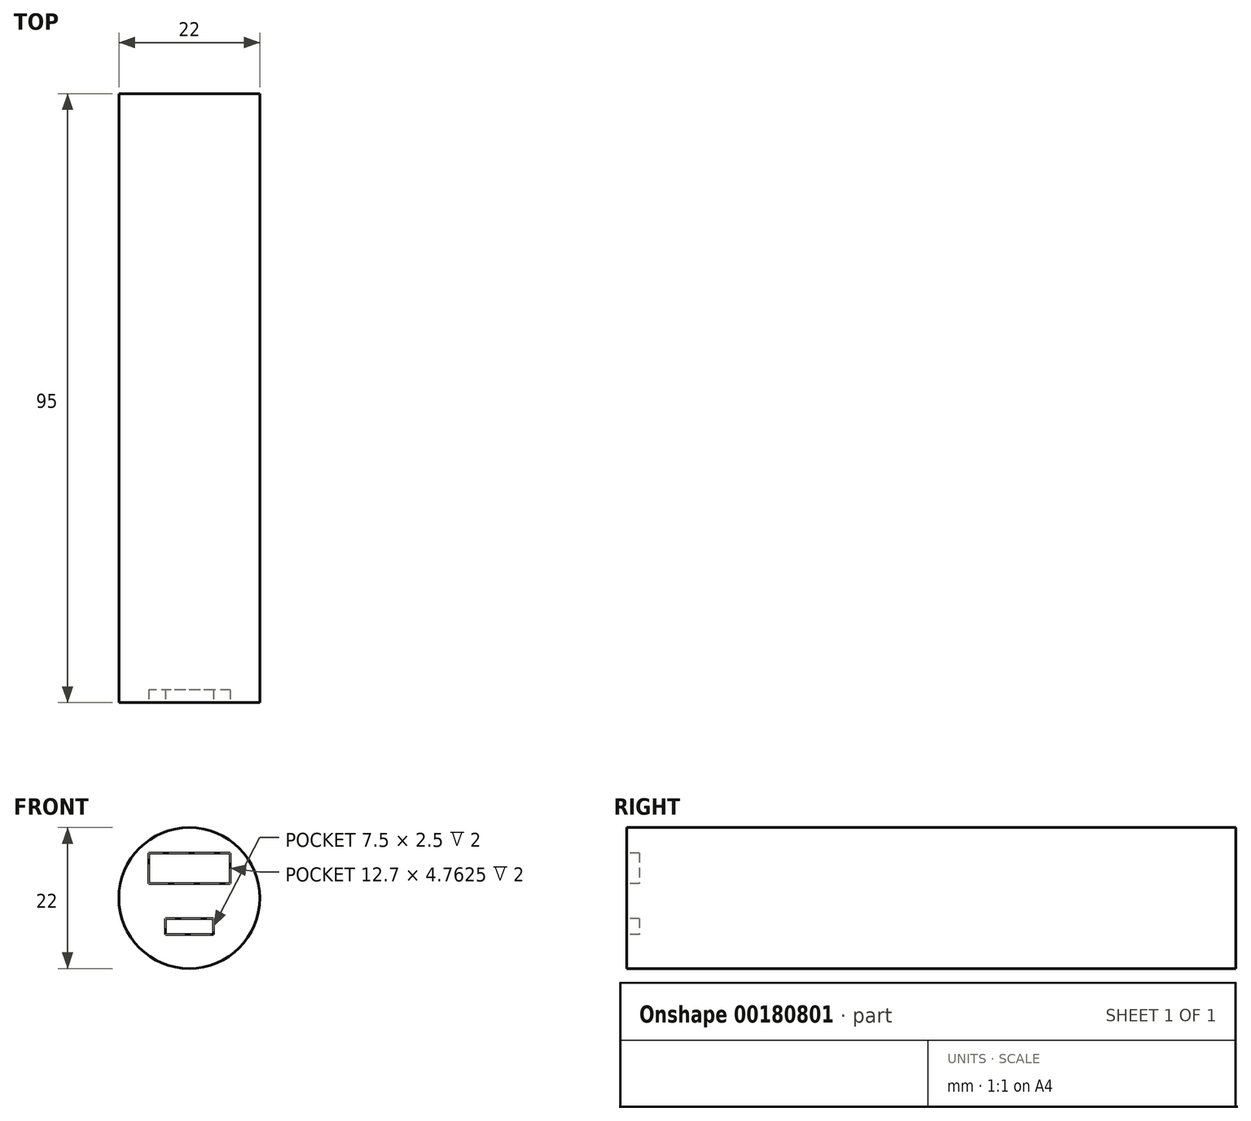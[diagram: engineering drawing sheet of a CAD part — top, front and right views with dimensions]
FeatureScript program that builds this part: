
annotation { "Feature Type Name" : "Feature", "Feature Type Description" : "" }
export const myFeature = defineFeature(function(context is Context, id is Id, definition is map)
    precondition{}
    {
        {
            var Q0;
            Q0=qCreatedBy(makeId("Front.planeOp"),FACE);
            var sketch = newSketch(context, id + "F0", { "sketchPlane" : qUnion([Q0])});
            skPoint(sketch, "E0.middle", {"position": v(0, 0) * mm});
            skCircle(sketch, "E1", {"center": v(0, 0) * mm, "radius": 11 * mm});
            skSolve(sketch);
        }
        {
            var Q0;
            Q0=makeQuery(id+"F0.imprint","IMPRINT",FACE,{"disambiguationData":[TD([[makeQuery(id+"F0.imprint","IMPRINT",EDGE,{"derivedFrom":sQuery(id+"F0.wireOp",EDGE,"E0.bottom")}),1.0]])]});
            var Q1;
            Q1=makeQuery(id+"F0.imprint","IMPRINT",FACE,{"disambiguationData":[TD([[makeQuery(id+"F0.imprint","IMPRINT",EDGE,{"derivedFrom":sQuery(id+"F0.wireOp",EDGE,"E1")}),1.0]])]});
            extrude(context, id + "F1", {"entities" : qUnion([Q0, Q1]), "depth" : 95 * mm, "offsetDistance" : 25 * mm});
        }
        {
            var Q0;
            Q0=makeQuery(id+"F1.opExtrude","CAP_FACE",FACE,{"disambiguationData":[OSD([sQuery(id+"F0.wireOp",EDGE,"E1")])],"isStart":false});
            var sketch = newSketch(context, id + "F2", { "sketchPlane" : qUnion([Q0])});
            skLineSegment(sketch, "E2.bottom", {"start": v(6.35, 7.02) * mm, "end": v(-6.35, 7.02) * mm});
            skLineSegment(sketch, "E2.top", {"start": v(6.35, 2.26) * mm, "end": v(-6.35, 2.26) * mm});
            skLineSegment(sketch, "E2.left", {"start": v(6.35, 7.02) * mm, "end": v(6.35, 2.26) * mm});
            skLineSegment(sketch, "E2.right", {"start": v(-6.35, 7.02) * mm, "end": v(-6.35, 2.26) * mm});
            skPoint(sketch, "E2.middle", {"position": v(0, 4.64) * mm});
            skLineSegment(sketch, "E3.bottom", {"start": v(3.75, -3.2) * mm, "end": v(-3.75, -3.2) * mm});
            skLineSegment(sketch, "E3.top", {"start": v(3.75, -5.7) * mm, "end": v(-3.75, -5.7) * mm});
            skLineSegment(sketch, "E3.left", {"start": v(3.75, -3.2) * mm, "end": v(3.75, -5.7) * mm});
            skLineSegment(sketch, "E3.right", {"start": v(-3.75, -3.2) * mm, "end": v(-3.75, -5.7) * mm});
            skPoint(sketch, "E3.middle", {"position": v(0, -4.45) * mm});
            skSolve(sketch);
        }
        {
            var Q0;
            Q0=makeQuery(id+"F2.imprint","IMPRINT",FACE,{"disambiguationData":[TD([[makeQuery(id+"F2.imprint","IMPRINT",EDGE,{"derivedFrom":sQuery(id+"F2.wireOp",EDGE,"E2.bottom")}),1.0]])]});
            var Q1;
            Q1=makeQuery(id+"F2.imprint","IMPRINT",FACE,{"disambiguationData":[TD([[makeQuery(id+"F2.imprint","IMPRINT",EDGE,{"derivedFrom":sQuery(id+"F2.wireOp",EDGE,"E3.bottom")}),1.0]])]});
            extrude(context, id + "F3", {"entities" : qUnion([Q0, Q1]), "operationType" : NewBodyOperationType.REMOVE, "oppositeDirection" : true, "depth" : 2 * mm, "offsetDistance" : 25 * mm});
        }
    });
